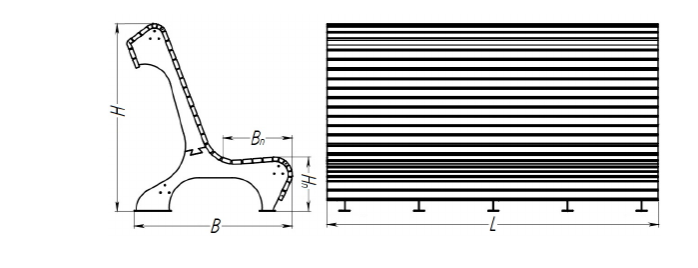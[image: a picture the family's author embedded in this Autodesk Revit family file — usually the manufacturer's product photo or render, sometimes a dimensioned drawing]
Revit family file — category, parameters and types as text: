
# Revit family: Скамейка стальная «Сафари» Арт 12196
name_source: partatom
category: Антураж
revit_build: Autodesk Revit 2018 (Build: 20180423_1000(x64)
units: mm (PartAtom-declared; Revit-internal decimal feet)

## family parameters
Всегда вертикально = Да
Источник визуального образа = Геометрия семейства
На основе рабочей плоскости = Нет
Общий = Нет
При загрузке вырезать с полостями = Нет
Точка расчета площади = Нет

## types (2) — shared parameters
URL = https://hobbyka.ru
Артикул товара = Арт. 12196
Высота = 1400 мм
Группа модели = Скамейки
Длина = 2500 мм
Изготовитель = ООО «Хоббика
Материал изделия = Сталь, дерево
Цвет лавки = Дерево
Цвет опоры = Сталь
Ширина = 1200 мм

## per-type parameters (varying)
| type | 3 опоры | 5 опор | Изображение типоразмера |
| Скамейка стальная «Сафари». Версия с 3-мя опорами | Да | Нет | Скамейка стальная «Сафари» Арт 12196 3 опоры.jpeg |
| Скамейка стальная «Сафари». Версия с 5-ю опорами | Нет | Да | Скамейка стальная «Сафари» Арт 12196 5 опор.jpg |

note: column(s) folded — value = type name in every type: Описание
